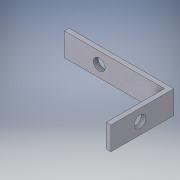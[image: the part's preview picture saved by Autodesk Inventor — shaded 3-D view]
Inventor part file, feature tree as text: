
AUTODESK INVENTOR PART (.ipt)
format: ipt  version: 2019 (Build 230136000, 136)  size: 117,760 bytes
history: native  units: in
note: dims shown in document units (in); Inventor stores cm internally (conversion verified against a paired STEP export)
features: extrude x4, sketch x4
ambient origin geometry x8: Origin, YZ Plane, XZ Plane, XY Plane, X Axis, Y Axis, Z Axis, Center Point
bodies: Solid1 (feature_tree)
feature tree (8):
  extrude  "Extrusion1"  Depth=0.0787in TaperAngle=0.0deg
  extrude  "Extrusion2"  Depth=0.9843in TaperAngle=0.0deg
  extrude  "Extrusion3"  [1 undecoded]
  extrude  "Extrusion4"  [1 undecoded]
  sketch  "Sketch1"  dims[d2=0.0787in d3=0.0in d7=0.0787in d8=0.0in]
  sketch  "Sketch2"  dims[d10=0.0787in d11=0.9843in d12=0.0in]
  sketch  "Sketch3"  dims[d15=0.9843in d16=0.0in]
  sketch  "Sketch4"
note: 2 required parameter values undecoded (feature->parameter linkage not recoverable at this tier; creation-order binding heuristic only, values carry confidence <= 0.55)
